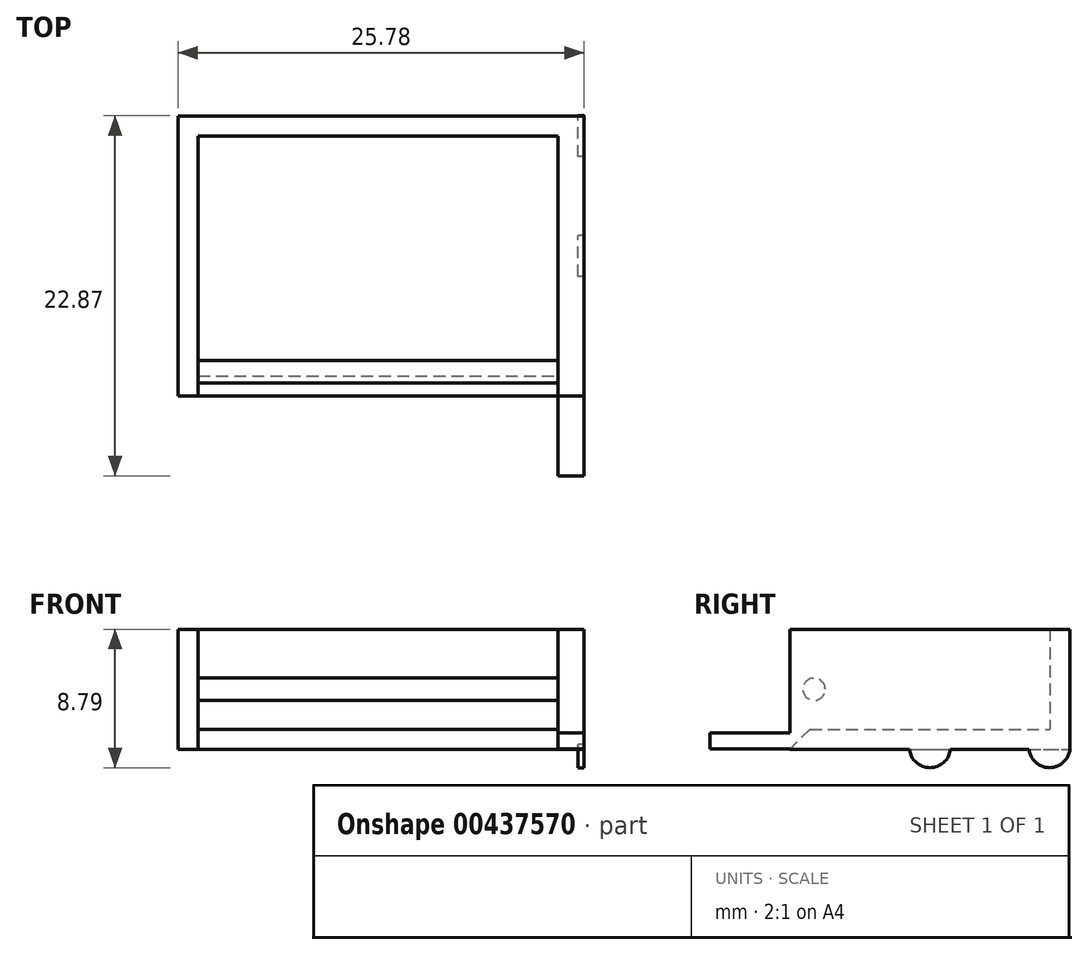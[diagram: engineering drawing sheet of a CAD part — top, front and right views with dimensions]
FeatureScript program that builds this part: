
annotation { "Feature Type Name" : "Feature", "Feature Type Description" : "" }
export const myFeature = defineFeature(function(context is Context, id is Id, definition is map)
    precondition{}
    {
        {
            var Q0;
            Q0=qCreatedBy(makeId("Front.planeOp"),FACE);
            var sketch = newSketch(context, id + "F0", { "sketchPlane" : qUnion([Q0])});
            skLineSegment(sketch, "E0.bottom", {"start": v(12.7, 3.81) * mm, "end": v(-12.7, 3.81) * mm});
            skLineSegment(sketch, "E0.top", {"start": v(12.7, -3.8) * mm, "end": v(-12.7, -3.8) * mm});
            skLineSegment(sketch, "E0.left", {"start": v(12.7, 3.8) * mm, "end": v(12.7, -3.8) * mm});
            skLineSegment(sketch, "E0.right", {"start": v(-12.7, 3.8) * mm, "end": v(-12.7, -3.8) * mm});
            skPoint(sketch, "E0.middle", {"position": v(0, 0) * mm});
            skSolve(sketch);
        }
        {
            var Q0;
            Q0=makeQuery(id+"F0.imprint","IMPRINT",FACE,{"disambiguationData":[TD([[makeQuery(id+"F0.imprint","IMPRINT",EDGE,{"derivedFrom":sQuery(id+"F0.wireOp",EDGE,"E0.bottom")}),1.0]])]});
            extrude(context, id + "F1", {"entities" : qUnion([Q0]), "endBound" : BoundingType.SYMMETRIC, "depth" : 17.78 * mm});
        }
        {
            var Q0;
            Q0=makeQuery(id+"F1.opExtrude","CAP_FACE",FACE,{"disambiguationData":[OSD([sQuery(id+"F0.wireOp",EDGE,"E0.bottom"),sQuery(id+"F0.wireOp",EDGE,"E0.top"),sQuery(id+"F0.wireOp",EDGE,"E0.left"),sQuery(id+"F0.wireOp",EDGE,"E0.right")])],"isStart":false});
            var Q1;
            Q1=makeQuery(id+"F1.opExtrude","SWEPT_FACE",FACE,{"disambiguationData":[OSD([sQuery(id+"F0.wireOp",EDGE,"E0.bottom")])]});
            shell(context, id + "F2", {"entities" : qUnion([Q0, Q1]), "thickness" : 1.27 * mm});
        }
        {
            var Q0;
            Q0=makeQuery(id+"F1.opExtrude","SWEPT_FACE",FACE,{"disambiguationData":[OSD([sQuery(id+"F0.wireOp",EDGE,"E0.left")])]});
            var sketch = newSketch(context, id + "F3", { "sketchPlane" : qUnion([Q0])});
            skCircle(sketch, "E1", {"center": v(-7.7, -3.67) * mm, "radius": 1.19 * mm});
            skCircle(sketch, "E2", {"center": v(0, -3.67) * mm, "radius": 1.3 * mm});
            skCircle(sketch, "E3", {"center": v(7.6, -3.67) * mm, "radius": 1.3 * mm});
            skSolve(sketch);
        }
        {
            var Q0;
            {var subQ0=sQuery(id+"F3.wireOp",EDGE,"E1");var subQ1=sQuery(id+"F0.wireOp",EDGE,"E0.left");var subQ2=makeQuery(id+"F1.opExtrude","CAP_EDGE",EDGE,{"disambiguationData":[OSD([subQ1])],"isStart":false});var subQ3=makeQuery(id+"F3.imprint","INTERSECT",VERTEX,{"disambiguationData":[OD(0.0)],"derivedFrom":[subQ2,subQ0]});Q0=makeQuery(id+"F3.imprint","IMPRINT",FACE,{"disambiguationData":[TD([[makeQuery(id+"F3.imprint","IMPRINT",EDGE,{"disambiguationData":[TD([[subQ3,1.0]])],"derivedFrom":subQ2}),1.0]])]});}
            var Q1;
            {var subQ0=sQuery(id+"F3.wireOp",EDGE,"E1");var subQ1=makeQuery(id+"F1.opExtrude","SWEPT_EDGE",EDGE,{"disambiguationData":[OSD([sQuery(id+"F0.wireOp",EDGE,"E0.top"),sQuery(id+"F0.wireOp",EDGE,"E0.left")])]});var subQ2=makeQuery(id+"F3.imprint","INTERSECT",VERTEX,{"disambiguationData":[OD(0.0)],"derivedFrom":[subQ1,subQ0]});Q1=makeQuery(id+"F3.imprint","IMPRINT",FACE,{"disambiguationData":[TD([[makeQuery(id+"F3.imprint","IMPRINT",EDGE,{"disambiguationData":[TD([[subQ2,-1.0]])],"derivedFrom":subQ0}),1.0]])]});}
            var Q2;
            {var subQ0=sQuery(id+"F3.wireOp",EDGE,"E2");var subQ1=makeQuery(id+"F1.opExtrude","SWEPT_EDGE",EDGE,{"disambiguationData":[OSD([sQuery(id+"F0.wireOp",EDGE,"E0.top"),sQuery(id+"F0.wireOp",EDGE,"E0.left")])]});var subQ2=makeQuery(id+"F3.imprint","INTERSECT",VERTEX,{"disambiguationData":[OD(0.0)],"derivedFrom":[subQ1,subQ0]});Q2=makeQuery(id+"F3.imprint","IMPRINT",FACE,{"disambiguationData":[TD([[makeQuery(id+"F3.imprint","IMPRINT",EDGE,{"disambiguationData":[TD([[subQ2,1.0]])],"derivedFrom":subQ0}),1.0]])]});}
            var Q3;
            {var subQ0=sQuery(id+"F3.wireOp",EDGE,"E2");var subQ1=makeQuery(id+"F1.opExtrude","SWEPT_EDGE",EDGE,{"disambiguationData":[OSD([sQuery(id+"F0.wireOp",EDGE,"E0.top"),sQuery(id+"F0.wireOp",EDGE,"E0.left")])]});var subQ2=makeQuery(id+"F3.imprint","INTERSECT",VERTEX,{"disambiguationData":[OD(0.0)],"derivedFrom":[subQ1,subQ0]});Q3=makeQuery(id+"F3.imprint","IMPRINT",FACE,{"disambiguationData":[TD([[makeQuery(id+"F3.imprint","IMPRINT",EDGE,{"disambiguationData":[TD([[subQ2,-1.0]])],"derivedFrom":subQ0}),1.0]])]});}
            var Q4;
            {var subQ0=sQuery(id+"F3.wireOp",EDGE,"E3");var subQ1=sQuery(id+"F0.wireOp",EDGE,"E0.left");var subQ2=makeQuery(id+"F1.opExtrude","CAP_EDGE",EDGE,{"disambiguationData":[OSD([subQ1])],"isStart":true});var subQ3=makeQuery(id+"F3.imprint","INTERSECT",VERTEX,{"derivedFrom":[subQ2,subQ0]});Q4=makeQuery(id+"F3.imprint","IMPRINT",FACE,{"disambiguationData":[TD([[makeQuery(id+"F3.imprint","IMPRINT",EDGE,{"disambiguationData":[TD([[subQ3,-1.0]])],"derivedFrom":subQ0}),1.0]])]});}
            var Q5;
            {var subQ0=sQuery(id+"F3.wireOp",EDGE,"E3");var subQ1=sQuery(id+"F0.wireOp",EDGE,"E0.left");var subQ2=makeQuery(id+"F1.opExtrude","CAP_EDGE",EDGE,{"disambiguationData":[OSD([subQ1])],"isStart":true});var subQ3=makeQuery(id+"F3.imprint","INTERSECT",VERTEX,{"derivedFrom":[subQ2,subQ0]});Q5=makeQuery(id+"F3.imprint","IMPRINT",FACE,{"disambiguationData":[TD([[makeQuery(id+"F3.imprint","IMPRINT",EDGE,{"disambiguationData":[TD([[subQ3,1.0]])],"derivedFrom":subQ0}),1.0]])]});}
            var Q6;
            {var subQ1=sQuery(id+"F0.wireOp",EDGE,"E0.left");var subQ11=makeQuery(id+"F1.opExtrude","SWEPT_EDGE",EDGE,{"disambiguationData":[OSD([sQuery(id+"F0.wireOp",EDGE,"E0.bottom"),subQ1])]});Q6=makeQuery(id+"F3.imprint","IMPRINT",FACE,{"disambiguationData":[TD([[makeQuery(id+"F3.imprint","IMPRINT",EDGE,{"derivedFrom":subQ11}),-1.0]])]});}
            extrude(context, id + "F4", {"entities" : qUnion([Q0, Q1, Q2, Q3, Q4, Q5, Q6]), "operationType" : NewBodyOperationType.ADD, "depth" : 0.38 * mm});
        }
        {
            var Q0;
            {var subQ0=sQuery(id+"F0.wireOp",EDGE,"E0.top");Q0=makeQuery(id+"F2.opShell","OFFSET_EDGE",EDGE,{"disambiguationData":[OSD([subQ0]),TDD([makeQuery(id+"F1.opExtrude","CAP_EDGE",EDGE,{"disambiguationData":[OSD([subQ0])],"isStart":false})])]});}
            chamfer(context, id + "F5", {"entities" : qUnion([Q0]), "width" : 1.27 * mm, "tangentPropagation" : true});
        }
        {
            var Q0;
            Q0=makeQuery(id+"F2.opShell","OFFSET_FACE",FACE,{"disambiguationData":[OSD([sQuery(id+"F0.wireOp",EDGE,"E0.right")])]});
            var sketch = newSketch(context, id + "F6", { "sketchPlane" : qUnion([Q0])});
            skCircle(sketch, "E4", {"center": v(-7.36, 0) * mm, "radius": 0.7 * mm});
            skSolve(sketch);
        }
        {
            var Q0;
            Q0=makeQuery(id+"F6.imprint","IMPRINT",FACE,{"disambiguationData":[TD([[makeQuery(id+"F6.imprint","IMPRINT",EDGE,{"derivedFrom":sQuery(id+"F6.wireOp",EDGE,"E4")}),1.0]])]});
            extrude(context, id + "F7", {"entities" : qUnion([Q0]), "operationType" : NewBodyOperationType.ADD, "depth" : 24.18 * mm});
        }
        {
            var Q0;
            Q0=makeQuery(id+"F4.opExtrude","CAP_FACE",FACE,{"disambiguationData":[OSD([sQuery(id+"F0.wireOp",EDGE,"E0.bottom"),sQuery(id+"F0.wireOp",EDGE,"E0.top"),sQuery(id+"F0.wireOp",EDGE,"E0.left"),sQuery(id+"F3.wireOp",EDGE,"E1"),sQuery(id+"F3.wireOp",EDGE,"E2"),sQuery(id+"F3.wireOp",EDGE,"E3")])],"isStart":false});
            var sketch = newSketch(context, id + "F8", { "sketchPlane" : qUnion([Q0])});
            skLineSegment(sketch, "E5.bottom", {"start": v(-8.9, -3.79) * mm, "end": v(-13.97, -3.79) * mm});
            skLineSegment(sketch, "E5.top", {"start": v(-8.9, -2.77) * mm, "end": v(-13.97, -2.77) * mm});
            skLineSegment(sketch, "E5.left", {"start": v(-8.9, -3.79) * mm, "end": v(-8.9, -2.77) * mm});
            skLineSegment(sketch, "E5.right", {"start": v(-13.97, -3.79) * mm, "end": v(-13.97, -2.77) * mm});
            skSolve(sketch);
        }
        {
            var Q0;
            Q0=makeQuery(id+"F8.imprint","IMPRINT",FACE,{"disambiguationData":[TD([[makeQuery(id+"F8.imprint","IMPRINT",EDGE,{"derivedFrom":sQuery(id+"F8.wireOp",EDGE,"E5.bottom")}),-1.0]])]});
            extrude(context, id + "F9", {"entities" : qUnion([Q0]), "operationType" : NewBodyOperationType.ADD, "oppositeDirection" : true, "depth" : 1.65 * mm});
        }
    });
